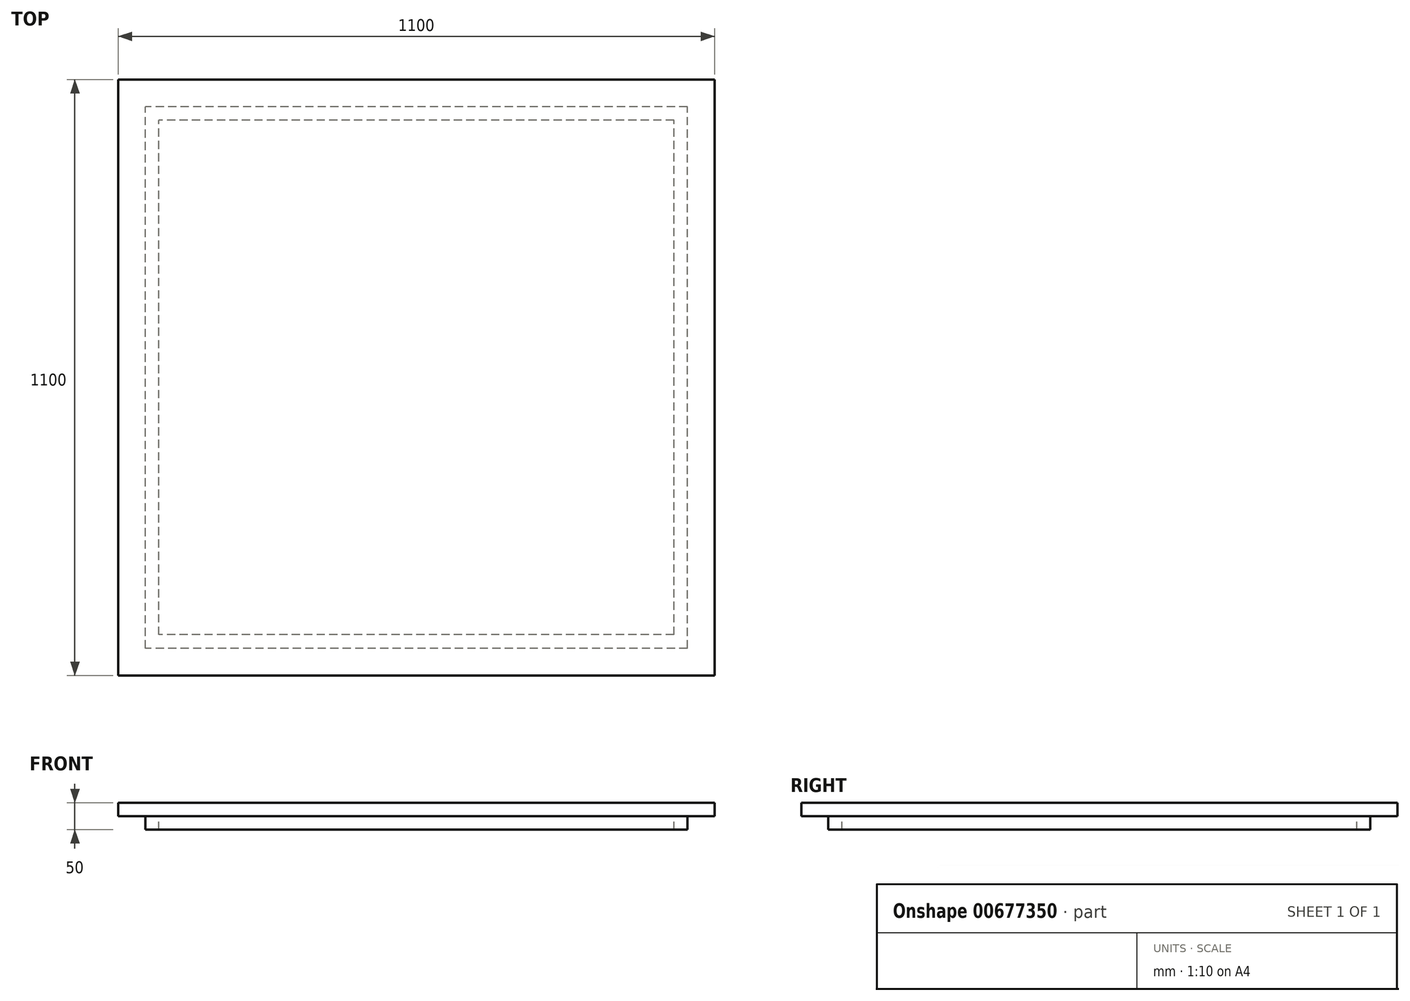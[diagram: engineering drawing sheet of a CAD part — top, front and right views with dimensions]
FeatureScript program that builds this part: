
annotation { "Feature Type Name" : "Feature", "Feature Type Description" : "" }
export const myFeature = defineFeature(function(context is Context, id is Id, definition is map)
    precondition{}
    {
        {
            var Q0;
            Q0=qCreatedBy(makeId("Top.planeOp"),FACE);
            var sketch = newSketch(context, id + "F0", { "sketchPlane" : qUnion([Q0])});
            skLineSegment(sketch, "E0.bottom", {"start": v(-550, 550) * mm, "end": v(550, 550) * mm});
            skLineSegment(sketch, "E0.top", {"start": v(-550, -550) * mm, "end": v(550, -550) * mm});
            skLineSegment(sketch, "E0.left", {"start": v(-550, 550) * mm, "end": v(-550, -550) * mm});
            skLineSegment(sketch, "E0.right", {"start": v(550, 550) * mm, "end": v(550, -550) * mm});
            skPoint(sketch, "E0.middle", {"position": v(0, 0) * mm});
            skSolve(sketch);
        }
        {
            var Q0;
            Q0=makeQuery(id+"F0.imprint","IMPRINT",FACE,{"disambiguationData":[TD([[makeQuery(id+"F0.imprint","IMPRINT",EDGE,{"derivedFrom":sQuery(id+"F0.wireOp",EDGE,"E0.bottom")}),-1.0]])]});
            extrude(context, id + "F1", {"entities" : qUnion([Q0]), "depth" : 25 * mm, "offsetDistance" : 25 * mm});
        }
        {
            var Q0;
            Q0=makeQuery(id+"F1.opExtrude","CAP_FACE",FACE,{"disambiguationData":[OSD([sQuery(id+"F0.wireOp",EDGE,"E0.bottom"),sQuery(id+"F0.wireOp",EDGE,"E0.top"),sQuery(id+"F0.wireOp",EDGE,"E0.left"),sQuery(id+"F0.wireOp",EDGE,"E0.right")])],"isStart":true});
            var sketch = newSketch(context, id + "F2", { "sketchPlane" : qUnion([Q0])});
            skLineSegment(sketch, "E1.bottom", {"start": v(500, 500) * mm, "end": v(-500, 500) * mm});
            skLineSegment(sketch, "E1.top", {"start": v(500, -500) * mm, "end": v(-500, -500) * mm});
            skLineSegment(sketch, "E1.left", {"start": v(500, 500) * mm, "end": v(500, -500) * mm});
            skLineSegment(sketch, "E1.right", {"start": v(-500, 500) * mm, "end": v(-500, -500) * mm});
            skPoint(sketch, "E1.middle", {"position": v(0, 0) * mm});
            skLineSegment(sketch, "E2.0", {"start": v(475, 475) * mm, "end": v(-475, 475) * mm});
            skLineSegment(sketch, "E2.1", {"start": v(475, 475) * mm, "end": v(475, -475) * mm});
            skLineSegment(sketch, "E2.2", {"start": v(475, -475) * mm, "end": v(-475, -475) * mm});
            skLineSegment(sketch, "E2.3", {"start": v(-475, 475) * mm, "end": v(-475, -475) * mm});
            skLineSegment(sketch, "E3.0", {"start": v(-314.22, 314.22) * mm, "end": v(-314.22, -314.22) * mm});
            skLineSegment(sketch, "E3.1", {"start": v(314.22, 314.22) * mm, "end": v(-314.22, 314.22) * mm});
            skLineSegment(sketch, "E3.2", {"start": v(314.22, -314.22) * mm, "end": v(314.22, 314.22) * mm});
            skLineSegment(sketch, "E3.3", {"start": v(-314.22, -314.22) * mm, "end": v(314.22, -314.22) * mm});
            skSolve(sketch);
        }
        {
            var Q0;
            Q0=makeQuery(id+"F2.imprint","IMPRINT",FACE,{"disambiguationData":[TD([[makeQuery(id+"F2.imprint","IMPRINT",EDGE,{"derivedFrom":sQuery(id+"F2.wireOp",EDGE,"E1.bottom")}),1.0]])]});
            extrude(context, id + "F3", {"entities" : qUnion([Q0]), "operationType" : NewBodyOperationType.ADD, "depth" : 25 * mm, "offsetDistance" : 25 * mm});
        }
    });
